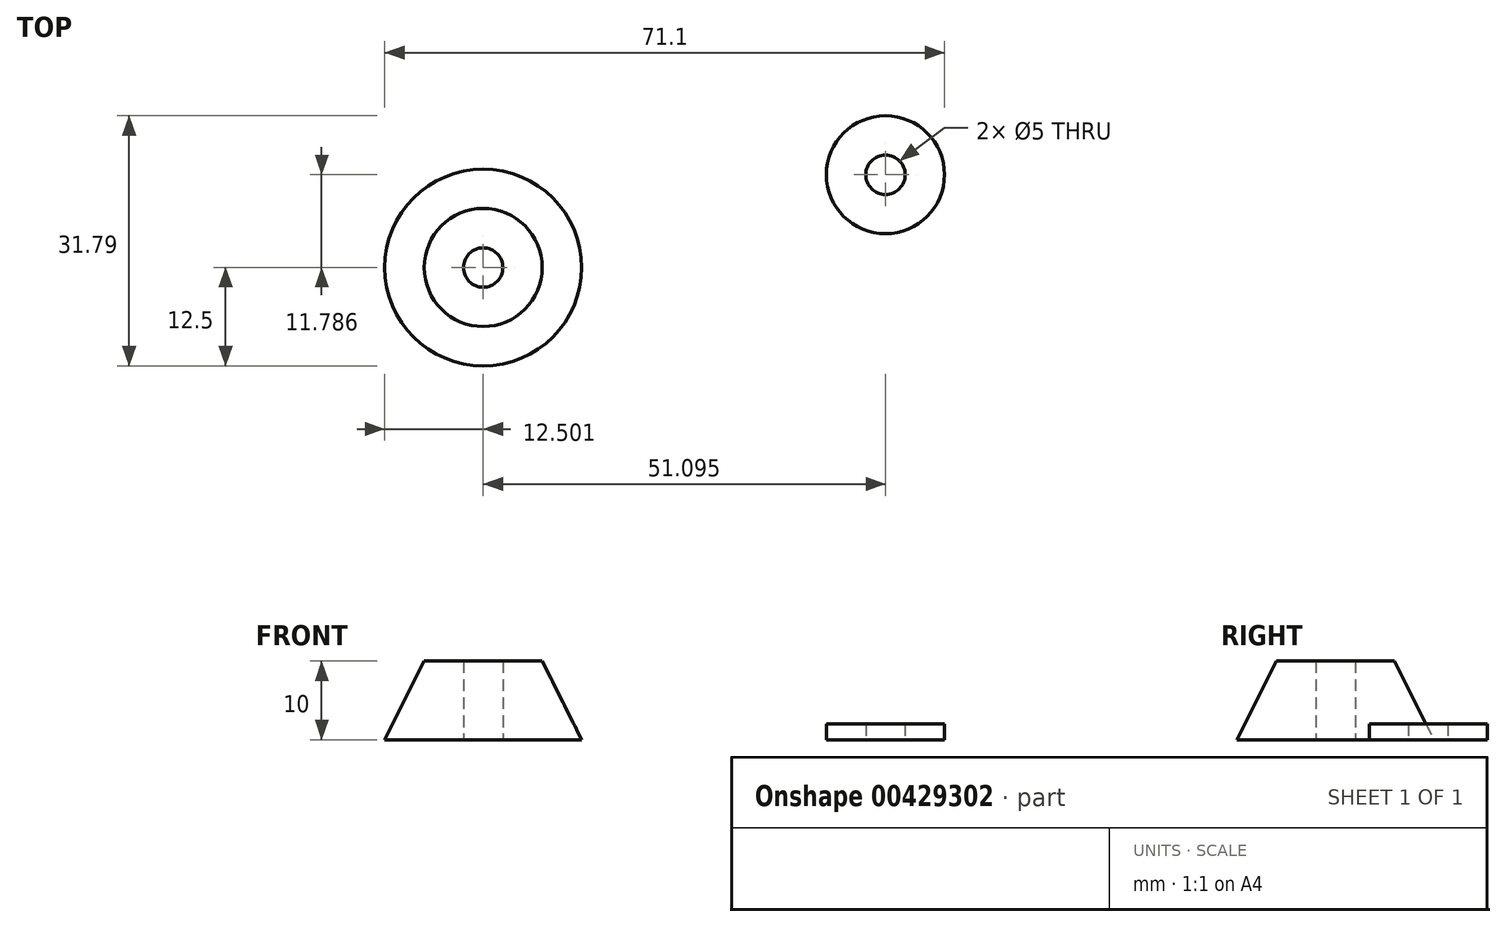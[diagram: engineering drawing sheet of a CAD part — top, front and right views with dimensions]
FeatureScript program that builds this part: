
annotation { "Feature Type Name" : "Feature", "Feature Type Description" : "" }
export const myFeature = defineFeature(function(context is Context, id is Id, definition is map)
    precondition{}
    {
        {
            var Q0;
            Q0=qCreatedBy(makeId("Top.planeOp"),FACE);
            var sketch = newSketch(context, id + "F0", { "sketchPlane" : qUnion([Q0])});
            skCircle(sketch, "E0", {"center": v(-34.03, 0) * mm, "radius": 2.5 * mm});
            skCircle(sketch, "E1", {"center": v(-34.03, 0) * mm, "radius": 12.5 * mm});
            skPoint(sketch, "E2", {"position": v(-21.53, 0) * mm});
            skPoint(sketch, "E3", {"position": v(-46.53, 0) * mm});
            skCircle(sketch, "E4", {"center": v(17.07, 11.79) * mm, "radius": 2.5 * mm});
            skCircle(sketch, "E5", {"center": v(17.07, 11.79) * mm, "radius": 7.5 * mm});
            skSolve(sketch);
        }
        {
            var Q0;
            Q0=makeQuery(id+"F0.imprint","IMPRINT",FACE,{"disambiguationData":[TD([[makeQuery(id+"F0.imprint","IMPRINT",EDGE,{"derivedFrom":sQuery(id+"F0.wireOp",EDGE,"E0")}),-1.0]])]});
            extrude(context, id + "F1", {"entities" : qUnion([Q0]), "depth" : 10 * mm});
        }
        {
            var Q0;
            Q0=makeQuery(id+"F0.imprint","IMPRINT",FACE,{"disambiguationData":[TD([[makeQuery(id+"F0.imprint","IMPRINT",EDGE,{"derivedFrom":sQuery(id+"F0.wireOp",EDGE,"E4")}),-1.0]])]});
            extrude(context, id + "F2", {"entities" : qUnion([Q0]), "depth" : 2 * mm});
        }
        {
            var Q0;
            Q0=makeQuery(id+"F1.opExtrude","CAP_EDGE",EDGE,{"disambiguationData":[OSD([sQuery(id+"F0.wireOp",EDGE,"E1")])],"isStart":false});
            chamfer(context, id + "F3", {"entities" : qUnion([Q0]), "chamferType" : ChamferType.TWO_OFFSETS, "width1" : 5 * mm, "oppositeDirection" : false, "width2" : 10 * mm, "tangentPropagation" : true});
        }
    });
